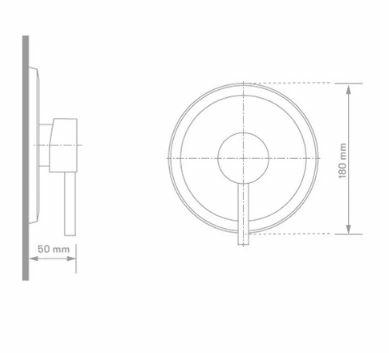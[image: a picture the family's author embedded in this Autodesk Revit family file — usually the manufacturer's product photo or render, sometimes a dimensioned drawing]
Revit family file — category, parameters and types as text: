
# Revit family: 01-2457-11 JABONERA REJILLA METALICA QUADRA
name_source: partatom
category: Plumbing Fixtures
revit_build: Autodesk Revit 2018 (Build: 20170223_1515(x64)
units: mm (PartAtom-declared; Revit-internal decimal feet)

## family parameters
Cut with Voids When Loaded = No
Host = Face
OmniClass Number = 23.31.11.00
Part Type = Normal
Room Calculation Point = No
Round Connector Dimension = Use Diameter
Shared = No

## types (1)
- 01-2457-11
    Alto Jabonera = 30 mm  [stored 0.0984252 ft]
    Ancho Soporte = 22 mm  [stored 0.0721785 ft]
    Ancho jabonera = 131 mm  [stored 0.42979 ft]
    CW Connection = Yes
    Default Elevation = 0 mm  [stored 0 ft]
    Description = JABONERA
    HW Connection = Yes
    Link Ficha Tecnica = http://infotecnica.gricol.com
    Manufacturer = Gricol
    Model = 01-2457-11
    Product Name = JABONERA REJILLA METALICA QUADRA
    Profundidad = 75 mm  [stored 0.246063 ft]
    Profundidad jabonera = 91 mm
    Soporte y Jabonera = Metal Laton Cromado
    Type Image = JABONERA REJILLA METALICA QUADRA.JPG
    URL = https://www.gricol.com
    Vent Connection = No
    Waste Connection = No

note: [stored X ft] marks values corroborated as IEEE doubles in the binary element streams (Revit-internal decimal feet)

## geometry (parser evidence)
native form markers: Blend x2, Sweep x4
no freeform markers — native parametric forms only
